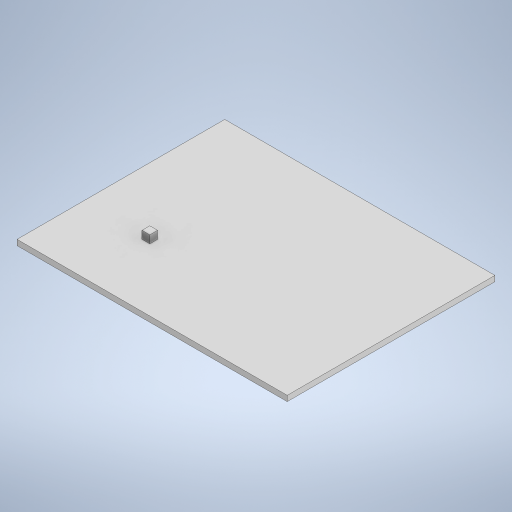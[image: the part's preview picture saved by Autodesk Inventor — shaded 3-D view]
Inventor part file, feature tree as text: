
AUTODESK INVENTOR PART (.ipt)
format: ipt  version: 2024.3 (Build 283343000, 343)  size: 220,160 bytes
history: native  units: mm
features: extrude x2, sketch x2, other x1
ambient origin geometry x8: Origin, YZ Plane, XZ Plane, XY Plane, X Axis, Y Axis, Z Axis, Center Point
bodies: Body1 (feature_tree)
feature tree (5):
  other  "Těleso1"
  extrude  "Vysunutí1"  Depth=133.0mm
  extrude  "Vysunutí2"  Depth=173.0mm
  sketch  "Náčrt1"
  sketch  "Náčrt2"
